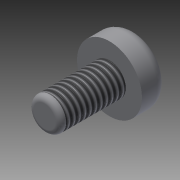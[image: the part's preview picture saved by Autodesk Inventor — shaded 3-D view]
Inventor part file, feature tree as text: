
AUTODESK INVENTOR PART (.ipt)
format: ipt  version: 2016 (Build 200138000, 138)  size: 137,728 bytes
history: native  units: mm
features: extrude x3, sketch x3, fillet x2, thread x1
ambient origin geometry x8: Origin, YZ Plane, XZ Plane, XY Plane, X Axis, Y Axis, Z Axis, Center Point
bodies: Solid1 (feature_tree)
feature tree (9):
  extrude  "Extrusion1"  Depth=6.0mm TaperAngle=0.0deg
  extrude  "Extrusion2"  Depth=2.4mm TaperAngle=0.0deg
  fillet  "Fillet4"  Radius=0.5mm
  thread  "Thread2"  [1 undecoded]
  fillet  "Fillet5"  Radius=1.0mm
  extrude  "Extrusion4"  Depth=1.0mm
  sketch  "Sketch1"  dims[d0=3.0mm d1=6.0mm d2=0.0mm]
  sketch  "Sketch2"  dims[d3=6.0mm d4=2.4mm d5=0.0mm d26=0.5mm d29=10.0mm d30=0.0mm d31=1.0mm]
  sketch  "Sketch5"  dims[d32=0.3mm d33=0.3mm d35=0.3mm d36=0.3mm d37=1.0mm d38=0.0mm]
note: 1 required parameter value undecoded (feature->parameter linkage not recoverable at this tier; creation-order binding heuristic only, values carry confidence <= 0.55)
